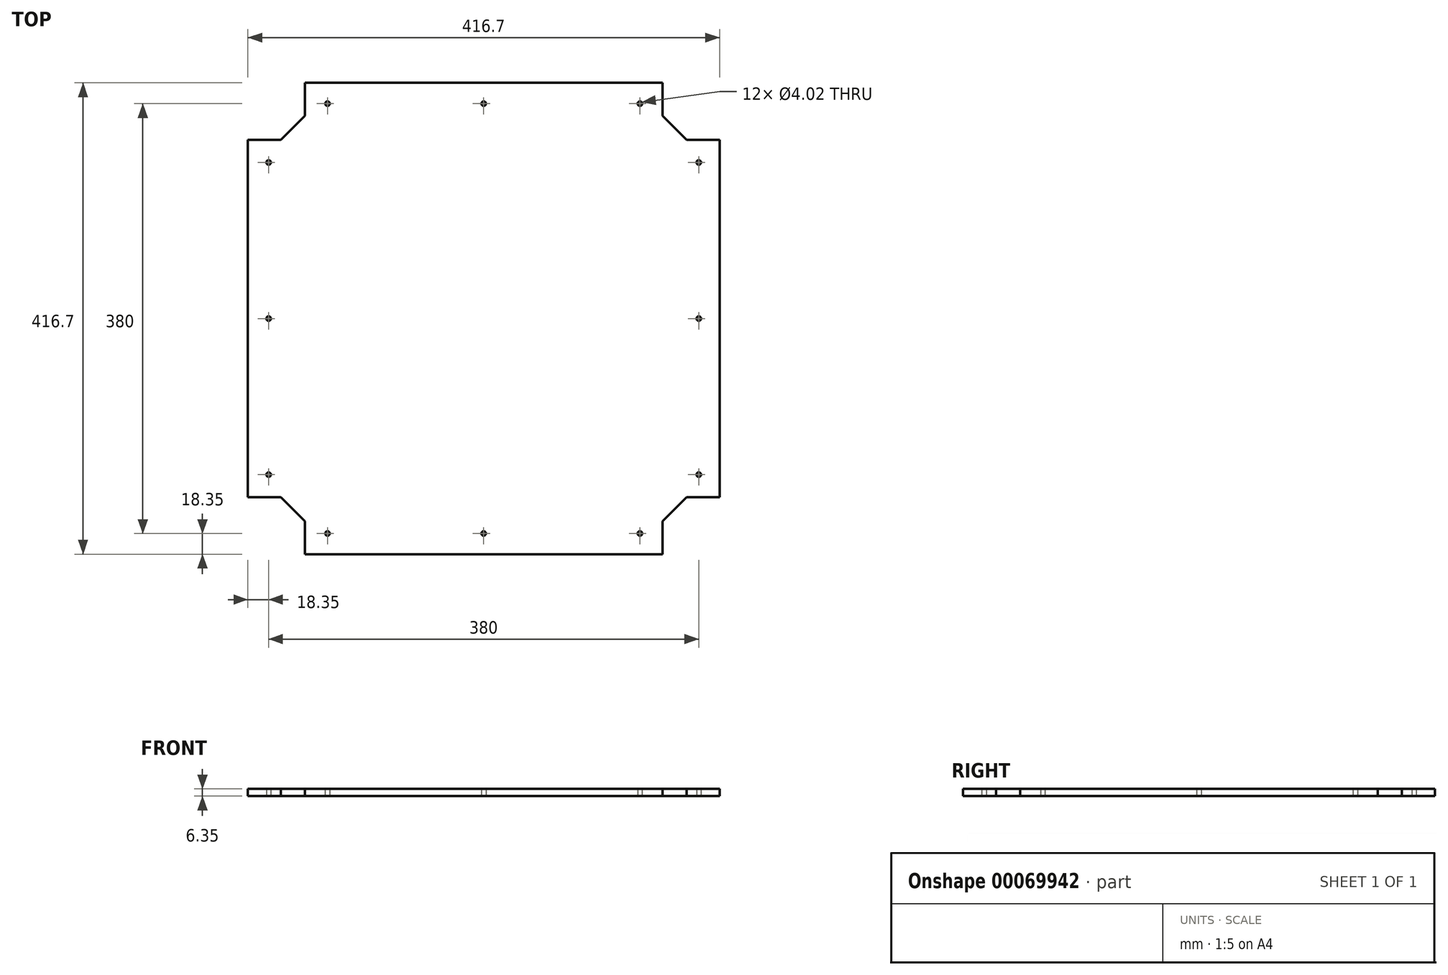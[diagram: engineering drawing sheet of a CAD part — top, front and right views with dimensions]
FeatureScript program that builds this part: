
annotation { "Feature Type Name" : "Feature", "Feature Type Description" : "" }
export const myFeature = defineFeature(function(context is Context, id is Id, definition is map)
    precondition{}
    {
        {
            var Q0;
            Q0=qCreatedBy(makeId("Top.planeOp"),FACE);
            var sketch = newSketch(context, id + "F0", { "sketchPlane" : qUnion([Q0])});
            skLineSegment(sketch, "E0", {"start": v(0, 0) * mm, "end": v(0, 180) * mm, "construction": true});
            skLineSegment(sketch, "E1", {"start": v(0, 180) * mm, "end": v(160, 180) * mm, "construction": true});
            skLineSegment(sketch, "E2", {"start": v(160, 180) * mm, "end": v(180, 160) * mm, "construction": true});
            skLineSegment(sketch, "E3", {"start": v(180, 160) * mm, "end": v(180, 0) * mm, "construction": true});
            skLineSegment(sketch, "E4", {"start": v(180, 0) * mm, "end": v(180, -160) * mm, "construction": true});
            skLineSegment(sketch, "E5", {"start": v(180, -160) * mm, "end": v(160, -180) * mm, "construction": true});
            skLineSegment(sketch, "E6", {"start": v(160, -180) * mm, "end": v(0, -180) * mm, "construction": true});
            skLineSegment(sketch, "E7", {"start": v(0, -180) * mm, "end": v(-160, -180) * mm, "construction": true});
            skLineSegment(sketch, "E8", {"start": v(-160, -180) * mm, "end": v(-180, -160) * mm, "construction": true});
            skLineSegment(sketch, "E9", {"start": v(-180, -160) * mm, "end": v(-180, 0) * mm, "construction": true});
            skLineSegment(sketch, "E10", {"start": v(-180, 0) * mm, "end": v(-180, 160) * mm, "construction": true});
            skLineSegment(sketch, "E11", {"start": v(-180, 160) * mm, "end": v(-160, 180) * mm, "construction": true});
            skLineSegment(sketch, "E12", {"start": v(-160, 180) * mm, "end": v(0, 180) * mm, "construction": true});
            skLineSegment(sketch, "E13", {"start": v(-180, 0) * mm, "end": v(0, 0) * mm, "construction": true});
            skLineSegment(sketch, "E14", {"start": v(0, 0) * mm, "end": v(180, 0) * mm, "construction": true});
            skLineSegment(sketch, "E15", {"start": v(0, 0) * mm, "end": v(0, -180) * mm, "construction": true});
            skLineSegment(sketch, "E16", {"start": v(-160, 180) * mm, "end": v(-160, 208.35) * mm, "construction": true});
            skLineSegment(sketch, "E17", {"start": v(-180, 160) * mm, "end": v(-208.35, 160) * mm, "construction": true});
            skLineSegment(sketch, "E18", {"start": v(160, 180) * mm, "end": v(160, 208.35) * mm, "construction": true});
            skLineSegment(sketch, "E19", {"start": v(180, 160) * mm, "end": v(208.35, 160) * mm, "construction": true});
            skLineSegment(sketch, "E20", {"start": v(180, -160) * mm, "end": v(208.35, -160) * mm, "construction": true});
            skLineSegment(sketch, "E21", {"start": v(160, -180) * mm, "end": v(160, -208.35) * mm, "construction": true});
            skLineSegment(sketch, "E22", {"start": v(-180, -160) * mm, "end": v(-208.35, -160) * mm, "construction": true});
            skLineSegment(sketch, "E23", {"start": v(-160, -180) * mm, "end": v(-160, -208.35) * mm, "construction": true});
            skLineSegment(sketch, "E24", {"start": v(-160, 194.17) * mm, "end": v(-158, 194.17) * mm, "construction": true});
            skLineSegment(sketch, "E25", {"start": v(-170, 170) * mm, "end": v(-168.59, 168.59) * mm, "construction": true});
            skLineSegment(sketch, "E26", {"start": v(-194.17, 160) * mm, "end": v(-194.17, 158) * mm, "construction": true});
            skLineSegment(sketch, "E27", {"start": v(160, 194.17) * mm, "end": v(158, 194.17) * mm, "construction": true});
            skLineSegment(sketch, "E28", {"start": v(170, 170) * mm, "end": v(168.59, 168.59) * mm, "construction": true});
            skLineSegment(sketch, "E29", {"start": v(194.17, 160) * mm, "end": v(194.17, 158) * mm, "construction": true});
            skLineSegment(sketch, "E30", {"start": v(194.17, -160) * mm, "end": v(194.17, -158) * mm, "construction": true});
            skLineSegment(sketch, "E31", {"start": v(170, -170) * mm, "end": v(168.59, -168.59) * mm, "construction": true});
            skLineSegment(sketch, "E32", {"start": v(160, -194.17) * mm, "end": v(158, -194.17) * mm, "construction": true});
            skLineSegment(sketch, "E33", {"start": v(-194.17, -160) * mm, "end": v(-194.17, -158) * mm, "construction": true});
            skLineSegment(sketch, "E34", {"start": v(-160, -194.18) * mm, "end": v(-158, -194.18) * mm, "construction": true});
            skLineSegment(sketch, "E35", {"start": v(-170, -170) * mm, "end": v(-168.59, -168.59) * mm, "construction": true});
            skLineSegment(sketch, "E36", {"start": v(-158, 194.17) * mm, "end": v(-158, 208.35) * mm});
            skLineSegment(sketch, "E37", {"start": v(-158, 208.35) * mm, "end": v(158, 208.35) * mm});
            skLineSegment(sketch, "E38", {"start": v(158, 208.35) * mm, "end": v(158, 194.17) * mm});
            skLineSegment(sketch, "E39", {"start": v(158, 194.17) * mm, "end": v(158, 179.17) * mm});
            skLineSegment(sketch, "E40", {"start": v(168.59, 168.59) * mm, "end": v(158, 179.17) * mm});
            skLineSegment(sketch, "E41", {"start": v(168.59, 168.59) * mm, "end": v(179.17, 158) * mm});
            skLineSegment(sketch, "E42", {"start": v(194.17, 158) * mm, "end": v(179.17, 158) * mm});
            skLineSegment(sketch, "E43", {"start": v(194.17, 158) * mm, "end": v(208.35, 158) * mm});
            skLineSegment(sketch, "E44", {"start": v(208.35, 158) * mm, "end": v(208.35, -158) * mm});
            skLineSegment(sketch, "E45", {"start": v(208.35, -158) * mm, "end": v(194.17, -158) * mm});
            skLineSegment(sketch, "E46", {"start": v(194.17, -158) * mm, "end": v(179.17, -158) * mm});
            skLineSegment(sketch, "E47", {"start": v(-208.35, 158) * mm, "end": v(-194.17, 158) * mm});
            skLineSegment(sketch, "E48", {"start": v(-194.17, 158) * mm, "end": v(-179.17, 158) * mm});
            skLineSegment(sketch, "E49", {"start": v(-208.35, 158) * mm, "end": v(-208.35, -158) * mm});
            skLineSegment(sketch, "E50", {"start": v(-208.35, -158) * mm, "end": v(-194.17, -158) * mm});
            skLineSegment(sketch, "E51", {"start": v(-194.17, -158) * mm, "end": v(-179.17, -158) * mm});
            skLineSegment(sketch, "E52", {"start": v(-168.59, -168.59) * mm, "end": v(-179.17, -158) * mm});
            skLineSegment(sketch, "E53", {"start": v(-168.59, -168.59) * mm, "end": v(-158, -179.17) * mm});
            skLineSegment(sketch, "E54", {"start": v(-158, -208.35) * mm, "end": v(-158, -194.18) * mm});
            skLineSegment(sketch, "E55", {"start": v(-158, -194.18) * mm, "end": v(-158, -179.17) * mm});
            skLineSegment(sketch, "E56", {"start": v(-158, -208.35) * mm, "end": v(158, -208.35) * mm});
            skLineSegment(sketch, "E57", {"start": v(158, -208.35) * mm, "end": v(158, -194.17) * mm});
            skLineSegment(sketch, "E58", {"start": v(158, -194.17) * mm, "end": v(158, -179.17) * mm});
            skLineSegment(sketch, "E59", {"start": v(168.59, -168.59) * mm, "end": v(158, -179.17) * mm});
            skLineSegment(sketch, "E60", {"start": v(168.59, -168.59) * mm, "end": v(179.17, -158) * mm});
            skLineSegment(sketch, "E61", {"start": v(-168.59, 168.59) * mm, "end": v(-179.17, 158) * mm});
            skLineSegment(sketch, "E62", {"start": v(-168.59, 168.59) * mm, "end": v(-158, 179.17) * mm});
            skLineSegment(sketch, "E63", {"start": v(-158, 194.17) * mm, "end": v(-158, 179.17) * mm});
            skLineSegment(sketch, "E64", {"start": v(-180, 0) * mm, "end": v(-190, 0) * mm, "construction": true});
            skLineSegment(sketch, "E65", {"start": v(-190, 0) * mm, "end": v(-190, 158) * mm, "construction": true});
            skLineSegment(sketch, "E66", {"start": v(-190, 0) * mm, "end": v(-190, -158) * mm, "construction": true});
            skPoint(sketch, "E66.endSnap0", {"position": v(-186.67, -158) * mm});
            skCircle(sketch, "E67", {"center": v(-190, -138) * mm, "radius": 2 * mm});
            skCircle(sketch, "E68", {"center": v(-190, 0) * mm, "radius": 2 * mm});
            skCircle(sketch, "E69", {"center": v(-190, 138) * mm, "radius": 2 * mm});
            skLineSegment(sketch, "E70", {"start": v(0, 180) * mm, "end": v(0, 190) * mm, "construction": true});
            skCircle(sketch, "E71", {"center": v(0, 190) * mm, "radius": 2 * mm});
            skCircle(sketch, "E72", {"center": v(-138, 190) * mm, "radius": 2 * mm});
            skCircle(sketch, "E73", {"center": v(138, 190) * mm, "radius": 2 * mm});
            skLineSegment(sketch, "E74", {"start": v(180, 0) * mm, "end": v(190, 0) * mm, "construction": true});
            skCircle(sketch, "E75", {"center": v(190, 0) * mm, "radius": 2 * mm});
            skCircle(sketch, "E76", {"center": v(190, -138) * mm, "radius": 2 * mm});
            skCircle(sketch, "E77", {"center": v(190, 138) * mm, "radius": 2 * mm});
            skLineSegment(sketch, "E78", {"start": v(0, -180) * mm, "end": v(0, -190) * mm, "construction": true});
            skCircle(sketch, "E79", {"center": v(0, -190) * mm, "radius": 2 * mm});
            skCircle(sketch, "E80", {"center": v(-138, -190) * mm, "radius": 2 * mm});
            skCircle(sketch, "E81", {"center": v(138, -190) * mm, "radius": 2 * mm});
            skLineSegment(sketch, "E82", {"start": v(-168.59, -168.59) * mm, "end": v(-154.44, -154.44) * mm, "construction": true});
            skLineSegment(sketch, "E83", {"start": v(168.59, -168.59) * mm, "end": v(154.44, -154.44) * mm, "construction": true});
            skPoint(sketch, "E84.orphan", {"position": v(-168.59, -160) * mm});
            skPoint(sketch, "E85.orphan", {"position": v(160, -170) * mm});
            skSolve(sketch);
        }
        {
            var Q0;
            Q0=makeQuery(id+"F0.imprint","IMPRINT",FACE,{"disambiguationData":[TD([[makeQuery(id+"F0.imprint","IMPRINT",EDGE,{"derivedFrom":sQuery(id+"F0.wireOp",EDGE,"E36")}),-1.0]])]});
            extrude(context, id + "F1", {"entities" : qUnion([Q0]), "depth" : 6.35 * mm});
        }
    });
